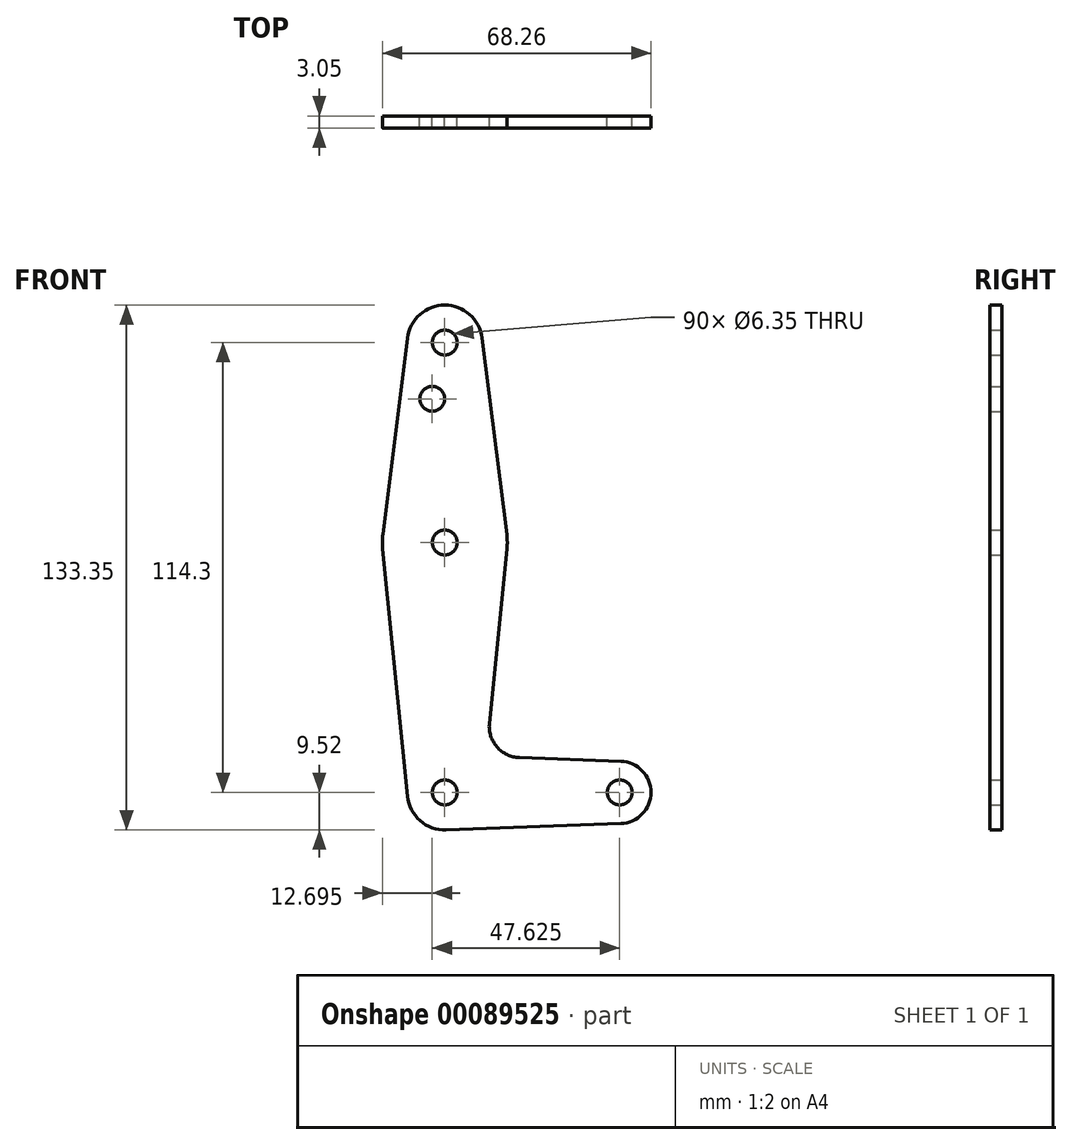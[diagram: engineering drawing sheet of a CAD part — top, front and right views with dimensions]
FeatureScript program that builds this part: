
annotation { "Feature Type Name" : "Feature", "Feature Type Description" : "" }
export const myFeature = defineFeature(function(context is Context, id is Id, definition is map)
    precondition{}
    {
        {
            var Q0;
            Q0=qCreatedBy(makeId("Front.planeOp"),FACE);
            var sketch = newSketch(context, id + "F0", { "sketchPlane" : qUnion([Q0])});
            skLineSegment(sketch, "E0", {"start": v(0, 114.3) * mm, "end": v(0, 0) * mm, "construction": true});
            skLineSegment(sketch, "E1", {"start": v(0, 0) * mm, "end": v(44.45, 0) * mm, "construction": true});
            skCircle(sketch, "E2", {"center": v(0, 0) * mm, "radius": 9.53 * mm});
            skCircle(sketch, "E3", {"center": v(44.45, 0) * mm, "radius": 7.94 * mm});
            skCircle(sketch, "E4", {"center": v(0, 114.3) * mm, "radius": 9.53 * mm});
            skCircle(sketch, "E5", {"center": v(0, 63.5) * mm, "radius": 15.88 * mm});
            skLineSegment(sketch, "E6", {"start": v(-9.45, 115.5) * mm, "end": v(-15.75, 65.48) * mm});
            skLineSegment(sketch, "E7.MirrorCS", {"start": v(9.45, 115.5) * mm, "end": v(15.75, 65.48) * mm});
            skLineSegment(sketch, "E8", {"start": v(-15.8, 61.91) * mm, "end": v(-9.48, -0.95) * mm});
            skLineSegment(sketch, "E9.MirrorCS", {"start": v(15.8, 61.91) * mm, "end": v(11.34, 17.58) * mm});
            skLineSegment(sketch, "E10", {"start": v(18.95, 8.85) * mm, "end": v(44.73, 7.93) * mm});
            skLineSegment(sketch, "E11.MirrorCS", {"start": v(0.34, -9.52) * mm, "end": v(44.73, -7.93) * mm});
            skCircle(sketch, "E12", {"center": v(0, 114.3) * mm, "radius": 3.18 * mm});
            skCircle(sketch, "E13", {"center": v(-3.18, 100.01) * mm, "radius": 3.18 * mm});
            skCircle(sketch, "E14", {"center": v(0, 63.5) * mm, "radius": 3.18 * mm});
            skCircle(sketch, "E15", {"center": v(0, 0) * mm, "radius": 3.18 * mm});
            skCircle(sketch, "E16", {"center": v(44.45, 0) * mm, "radius": 3.18 * mm});
            skPoint(sketch, "E17.newPointA", {"position": v(9.48, -0.95) * mm});
            skPoint(sketch, "E17.newPointB", {"position": v(0.34, 9.52) * mm});
            skArc(sketch, "E17.filletArc", {"start": v(11.34, 17.58) * mm, "mid": v(13.26, 11.57) * mm, "end": v(18.95, 8.85) * mm});
            skSolve(sketch);
        }
        {
            var Q0;
            {var subQ1=sQuery(id+"F0.wireOp",EDGE,"E6");Q0=makeQuery(id+"F0.imprint","IMPRINT",FACE,{"disambiguationData":[TD([[makeQuery(id+"F0.imprint","IMPRINT",EDGE,{"derivedFrom":subQ1}),1.0]])]});}
            var Q1;
            Q1=makeQuery(id+"F0.imprint","IMPRINT",FACE,{"disambiguationData":[TD([[makeQuery(id+"F0.imprint","IMPRINT",EDGE,{"derivedFrom":sQuery(id+"F0.wireOp",EDGE,"E12")}),-1.0]])]});
            var Q2;
            {var subQ0=sQuery(id+"F0.wireOp",EDGE,"E8");Q2=makeQuery(id+"F0.imprint","IMPRINT",FACE,{"disambiguationData":[TD([[makeQuery(id+"F0.imprint","IMPRINT",EDGE,{"derivedFrom":subQ0}),1.0]])]});}
            var Q3;
            Q3=makeQuery(id+"F0.imprint","IMPRINT",FACE,{"disambiguationData":[TD([[makeQuery(id+"F0.imprint","IMPRINT",EDGE,{"derivedFrom":sQuery(id+"F0.wireOp",EDGE,"E14")}),-1.0]])]});
            var Q4;
            Q4=makeQuery(id+"F0.imprint","IMPRINT",FACE,{"disambiguationData":[TD([[makeQuery(id+"F0.imprint","IMPRINT",EDGE,{"derivedFrom":sQuery(id+"F0.wireOp",EDGE,"E15")}),-1.0]])]});
            var Q5;
            Q5=makeQuery(id+"F0.imprint","IMPRINT",FACE,{"disambiguationData":[TD([[makeQuery(id+"F0.imprint","IMPRINT",EDGE,{"derivedFrom":sQuery(id+"F0.wireOp",EDGE,"E16")}),-1.0]])]});
            extrude(context, id + "F1", {"entities" : qUnion([Q0, Q1, Q2, Q3, Q4, Q5]), "depth" : 3.05 * mm});
        }
    });
